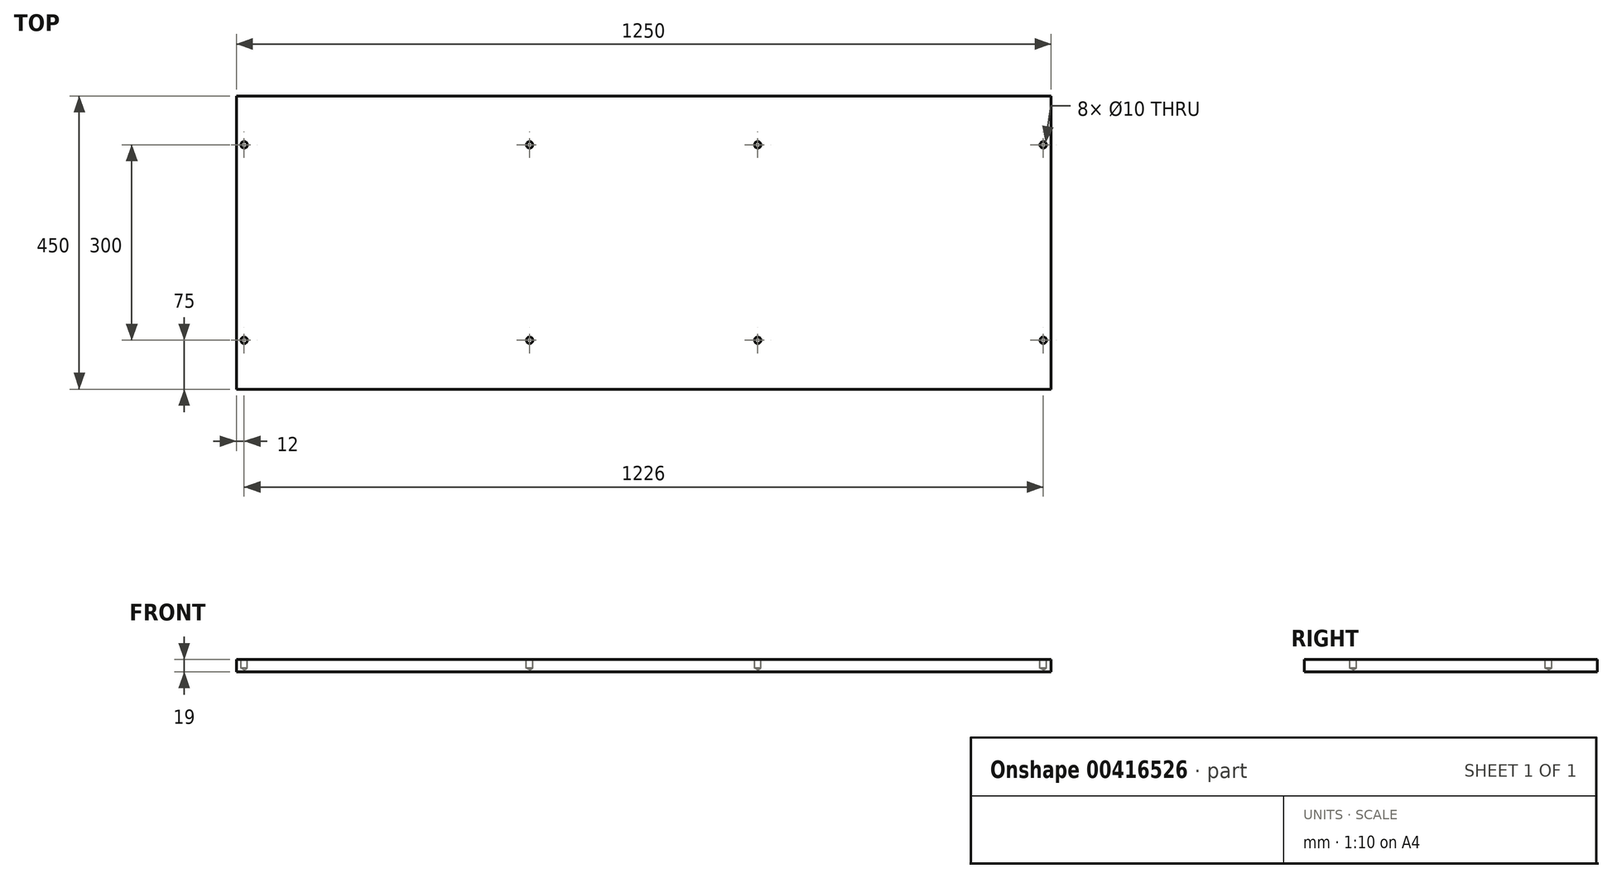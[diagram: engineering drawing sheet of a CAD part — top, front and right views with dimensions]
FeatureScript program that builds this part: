
annotation { "Feature Type Name" : "Feature", "Feature Type Description" : "" }
export const myFeature = defineFeature(function(context is Context, id is Id, definition is map)
    precondition{}
    {
        {
            var Q0;
            Q0=qCreatedBy(makeId("Top.planeOp"),FACE);
            var sketch = newSketch(context, id + "F0", { "sketchPlane" : qUnion([Q0])});
            skLineSegment(sketch, "E0.bottom", {"start": v(-625, 225) * mm, "end": v(625, 225) * mm});
            skLineSegment(sketch, "E0.top", {"start": v(-625, -225) * mm, "end": v(625, -225) * mm});
            skLineSegment(sketch, "E0.left", {"start": v(-625, 225) * mm, "end": v(-625, -225) * mm});
            skLineSegment(sketch, "E0.right", {"start": v(625, 225) * mm, "end": v(625, -225) * mm});
            skPoint(sketch, "E0.middle", {"position": v(0, 0) * mm});
            skSolve(sketch);
        }
        {
            var Q0;
            Q0=makeQuery(id+"F0.imprint","IMPRINT",FACE,{"disambiguationData":[TD([[makeQuery(id+"F0.imprint","IMPRINT",EDGE,{"derivedFrom":sQuery(id+"F0.wireOp",EDGE,"E0.bottom")}),-1.0]])]});
            extrude(context, id + "F1", {"entities" : qUnion([Q0]), "depth" : 19 * mm});
        }
        {
            var Q0;
            Q0=makeQuery(id+"F1.opExtrude","CAP_FACE",FACE,{"disambiguationData":[OSD([sQuery(id+"F0.wireOp",EDGE,"E0.bottom"),sQuery(id+"F0.wireOp",EDGE,"E0.top"),sQuery(id+"F0.wireOp",EDGE,"E0.left"),sQuery(id+"F0.wireOp",EDGE,"E0.right")])],"isStart":false});
            var sketch = newSketch(context, id + "F2", { "sketchPlane" : qUnion([Q0])});
            skLineSegment(sketch, "E1", {"start": v(-652.05, 150) * mm, "end": v(666.13, 150) * mm, "construction": true});
            skLineSegment(sketch, "E2", {"start": v(-647.41, -150) * mm, "end": v(666.13, -150) * mm, "construction": true});
            skLineSegment(sketch, "E3", {"start": v(-613, 238.42) * mm, "end": v(-613, -255.9) * mm, "construction": true});
            skLineSegment(sketch, "E4", {"start": v(-175, 238.42) * mm, "end": v(-175, -258.21) * mm, "construction": true});
            skLineSegment(sketch, "E5", {"start": v(175, 244.23) * mm, "end": v(175, -264.02) * mm, "construction": true});
            skLineSegment(sketch, "E6", {"start": v(613, 240.74) * mm, "end": v(613, -254.73) * mm, "construction": true});
            skPoint(sketch, "E7", {"position": v(-175, 150) * mm});
            skPoint(sketch, "E8", {"position": v(175, 150) * mm});
            skPoint(sketch, "E9", {"position": v(613, 150) * mm});
            skPoint(sketch, "E10", {"position": v(613, -150) * mm});
            skPoint(sketch, "E11", {"position": v(175, -150) * mm});
            skPoint(sketch, "E12", {"position": v(-613, 150) * mm});
            skPoint(sketch, "E13", {"position": v(-613, -150) * mm});
            skPoint(sketch, "E14", {"position": v(-175, -150) * mm});
            skSolve(sketch);
        }
        {
            var Q0;
            Q0=sQuery(id+"F2.wireOp",VERTEX,"E12");
            var Q1;
            Q1=sQuery(id+"F2.wireOp",VERTEX,"E7");
            var Q2;
            Q2=sQuery(id+"F2.wireOp",VERTEX,"E8");
            var Q3;
            Q3=sQuery(id+"F2.wireOp",VERTEX,"E9");
            var Q4;
            Q4=sQuery(id+"F2.wireOp",VERTEX,"E10");
            var Q5;
            Q5=sQuery(id+"F2.wireOp",VERTEX,"E11");
            var Q6;
            Q6=sQuery(id+"F2.wireOp",VERTEX,"E14");
            var Q7;
            Q7=sQuery(id+"F2.wireOp",VERTEX,"E13");
            var Q8;
            Q8=makeQuery(id+"F1.opExtrude","SWEPT_BODY",BODY,{"disambiguationData":[OSD([sQuery(id+"F0.wireOp",EDGE,"E0.bottom"),sQuery(id+"F0.wireOp",EDGE,"E0.top"),sQuery(id+"F0.wireOp",EDGE,"E0.left"),sQuery(id+"F0.wireOp",EDGE,"E0.right")])]});
            hole(context, id + "F3", {"style" : HoleStyle.SIMPLE, "endStyle" : HoleEndStyle.BLIND, "holeDiameter" : 10 * mm, "holeDepth" : 13 * mm, "isTappedThrough" : true, "tappedDepth" : 12 * mm, "tapClearance" : 3, "startFromSketch" : true, "locations" : qUnion([Q0, Q1, Q2, Q3, Q4, Q5, Q6, Q7]), "scope" : qUnion([Q8])});
        }
    });
